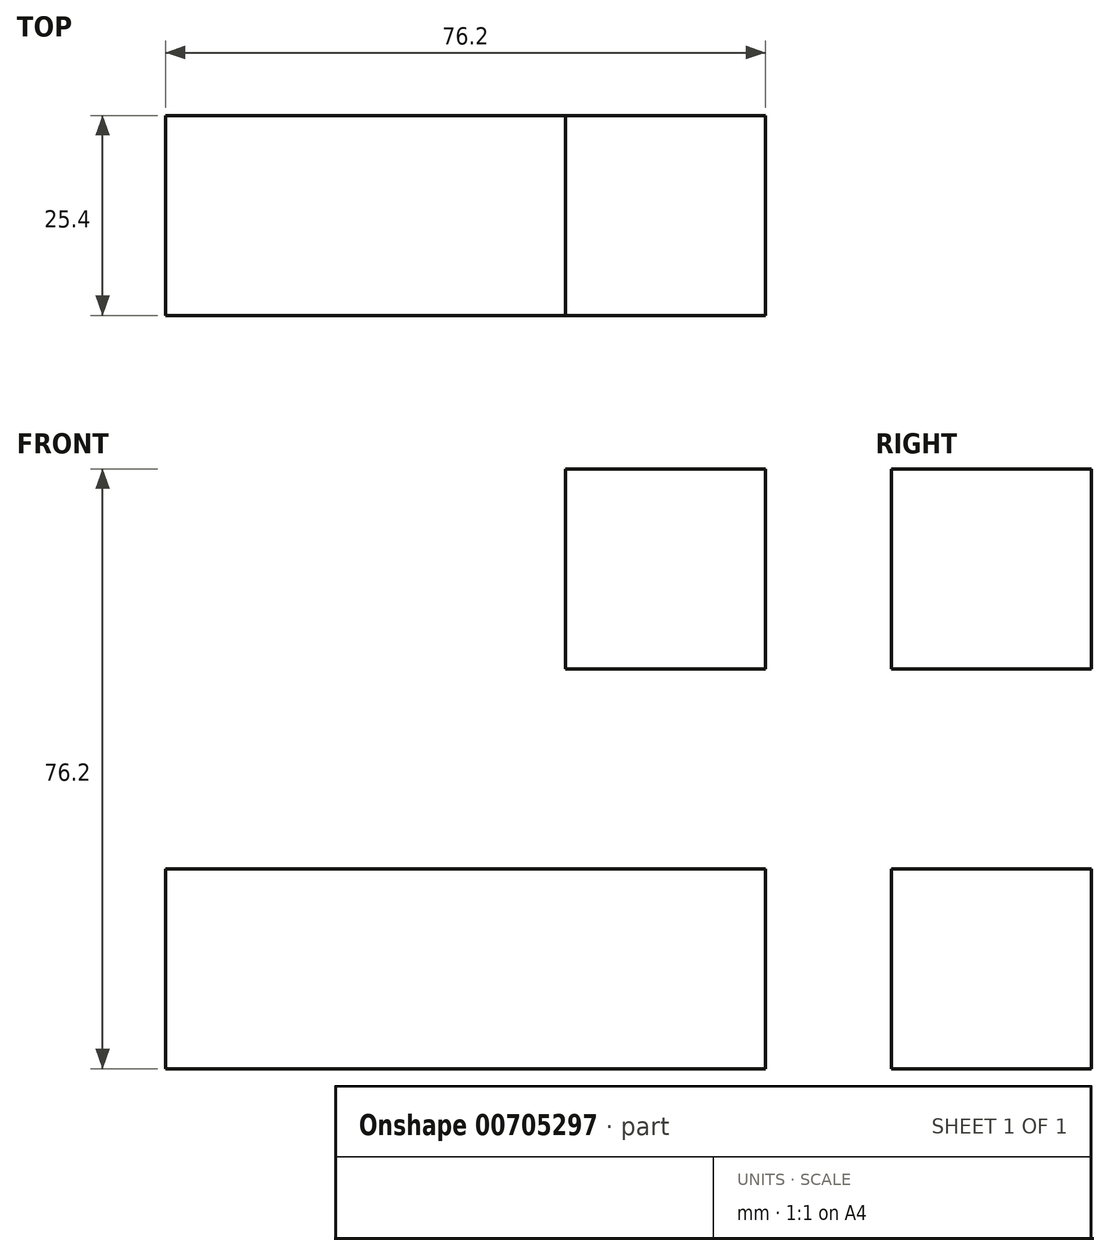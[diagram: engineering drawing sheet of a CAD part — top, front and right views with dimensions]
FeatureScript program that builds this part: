
annotation { "Feature Type Name" : "Feature", "Feature Type Description" : "" }
export const myFeature = defineFeature(function(context is Context, id is Id, definition is map)
    precondition{}
    {
        {
            var Q0;
            Q0=qCreatedBy(makeId("Front.planeOp"),FACE);
            var sketch = newSketch(context, id + "F0", { "sketchPlane" : qUnion([Q0])});
            skLineSegment(sketch, "E0.bottom", {"start": v(-25.4, 25.4) * mm, "end": v(0, 25.4) * mm});
            skLineSegment(sketch, "E0.top", {"start": v(-25.4, 0) * mm, "end": v(0, 0) * mm});
            skLineSegment(sketch, "E0.left", {"start": v(-25.4, 25.4) * mm, "end": v(-25.4, 0) * mm});
            skLineSegment(sketch, "E0.right", {"start": v(0, 25.4) * mm, "end": v(0, 0) * mm});
            skLineSegment(sketch, "E1.bottom", {"start": v(0, 25.4) * mm, "end": v(-25.4, 25.4) * mm});
            skLineSegment(sketch, "E1.top", {"start": v(0, 50.8) * mm, "end": v(-25.4, 50.8) * mm});
            skLineSegment(sketch, "E1.left", {"start": v(0, 25.4) * mm, "end": v(0, 50.8) * mm});
            skLineSegment(sketch, "E1.right", {"start": v(-25.4, 25.4) * mm, "end": v(-25.4, 50.8) * mm});
            skLineSegment(sketch, "E2.top", {"start": v(0, 76.2) * mm, "end": v(-25.4, 76.2) * mm});
            skLineSegment(sketch, "E2.left", {"start": v(0, 50.8) * mm, "end": v(0, 76.2) * mm});
            skLineSegment(sketch, "E2.right", {"start": v(-25.4, 50.8) * mm, "end": v(-25.4, 76.2) * mm});
            skLineSegment(sketch, "E3.bottom", {"start": v(-25.4, 25.4) * mm, "end": v(-50.8, 25.4) * mm});
            skLineSegment(sketch, "E3.top", {"start": v(-25.4, 0) * mm, "end": v(-50.8, 0) * mm});
            skLineSegment(sketch, "E3.right", {"start": v(-50.8, 25.4) * mm, "end": v(-50.8, 0) * mm});
            skLineSegment(sketch, "E4.bottom", {"start": v(-50.8, 25.4) * mm, "end": v(-76.2, 25.4) * mm});
            skLineSegment(sketch, "E4.top", {"start": v(-50.8, 0) * mm, "end": v(-76.2, 0) * mm});
            skLineSegment(sketch, "E4.right", {"start": v(-76.2, 25.4) * mm, "end": v(-76.2, 0) * mm});
            skSolve(sketch);
        }
        {
            var Q0;
            Q0=makeQuery(id+"F0.imprint","IMPRINT",FACE,{"disambiguationData":[TD([[makeQuery(id+"F0.imprint","IMPRINT",EDGE,{"derivedFrom":sQuery(id+"F0.wireOp",EDGE,"E3.bottom")}),1.0]])]});
            var Q1;
            Q1=makeQuery(id+"F0.imprint","IMPRINT",FACE,{"disambiguationData":[TD([[makeQuery(id+"F0.imprint","IMPRINT",EDGE,{"derivedFrom":sQuery(id+"F0.wireOp",EDGE,"E0.top")}),1.0]])]});
            var Q2;
            Q2=makeQuery(id+"F0.imprint","IMPRINT",FACE,{"disambiguationData":[TD([[makeQuery(id+"F0.imprint","IMPRINT",EDGE,{"derivedFrom":sQuery(id+"F0.wireOp",EDGE,"E1.bottom")}),-1.0]])]});
            var Q3;
            Q3=makeQuery(id+"F0.imprint","IMPRINT",FACE,{"disambiguationData":[TD([[makeQuery(id+"F0.imprint","IMPRINT",EDGE,{"derivedFrom":sQuery(id+"F0.wireOp",EDGE,"E1.top")}),-1.0]])]});
            var Q4;
            Q4=makeQuery(id+"F0.imprint","IMPRINT",FACE,{"disambiguationData":[TD([[makeQuery(id+"F0.imprint","IMPRINT",EDGE,{"derivedFrom":sQuery(id+"F0.wireOp",EDGE,"E4.bottom")}),1.0]])]});
            extrude(context, id + "F1", {"entities" : qUnion([Q0, Q1, Q2, Q3, Q4]), "depth" : 25.4 * mm, "offsetDistance" : 25.4 * mm});
        }
    });
